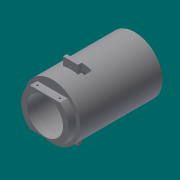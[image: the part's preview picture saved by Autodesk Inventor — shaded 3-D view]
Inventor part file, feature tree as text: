
AUTODESK INVENTOR PART (.ipt)
format: ipt  version: 2013 (Build 170138000, 138)  size: 215,040 bytes
history: native  units: mm
features: sketch x7, extrude x6, other x3, revolve x1, mirror x1
ambient origin geometry x8: Origin, YZ Plane, XZ Plane, XY Plane, X Axis, Y Axis, Z Axis, Center Point
feature tree (18):
  other  "ソリッド1"
  revolve  "回転1"
  other  "作業平面4"
  sketch  "スケッチ2"
  extrude  "押し出し1"  Depth=32.0mm
  extrude  "押し出し2"  Depth=30.0mm
  extrude  "押し出し3"  Depth=35.0mm
  extrude  "押し出し4"  Depth=2.0mm
  extrude  "押し出し5"  Depth=80.0mm
  mirror  "ミラー1"
  other  "作業平面5"
  extrude  "押し出し7"  TaperAngle=90.0deg  [1 undecoded]
  sketch  "スケッチ1"
  sketch  "スケッチ4"
  sketch  "スケッチ5"
  sketch  "スケッチ6"
  sketch  "スケッチ7"
  sketch  "スケッチ8"
note: 1 required parameter value undecoded (feature->parameter linkage not recoverable at this tier; creation-order binding heuristic only, values carry confidence <= 0.55)
